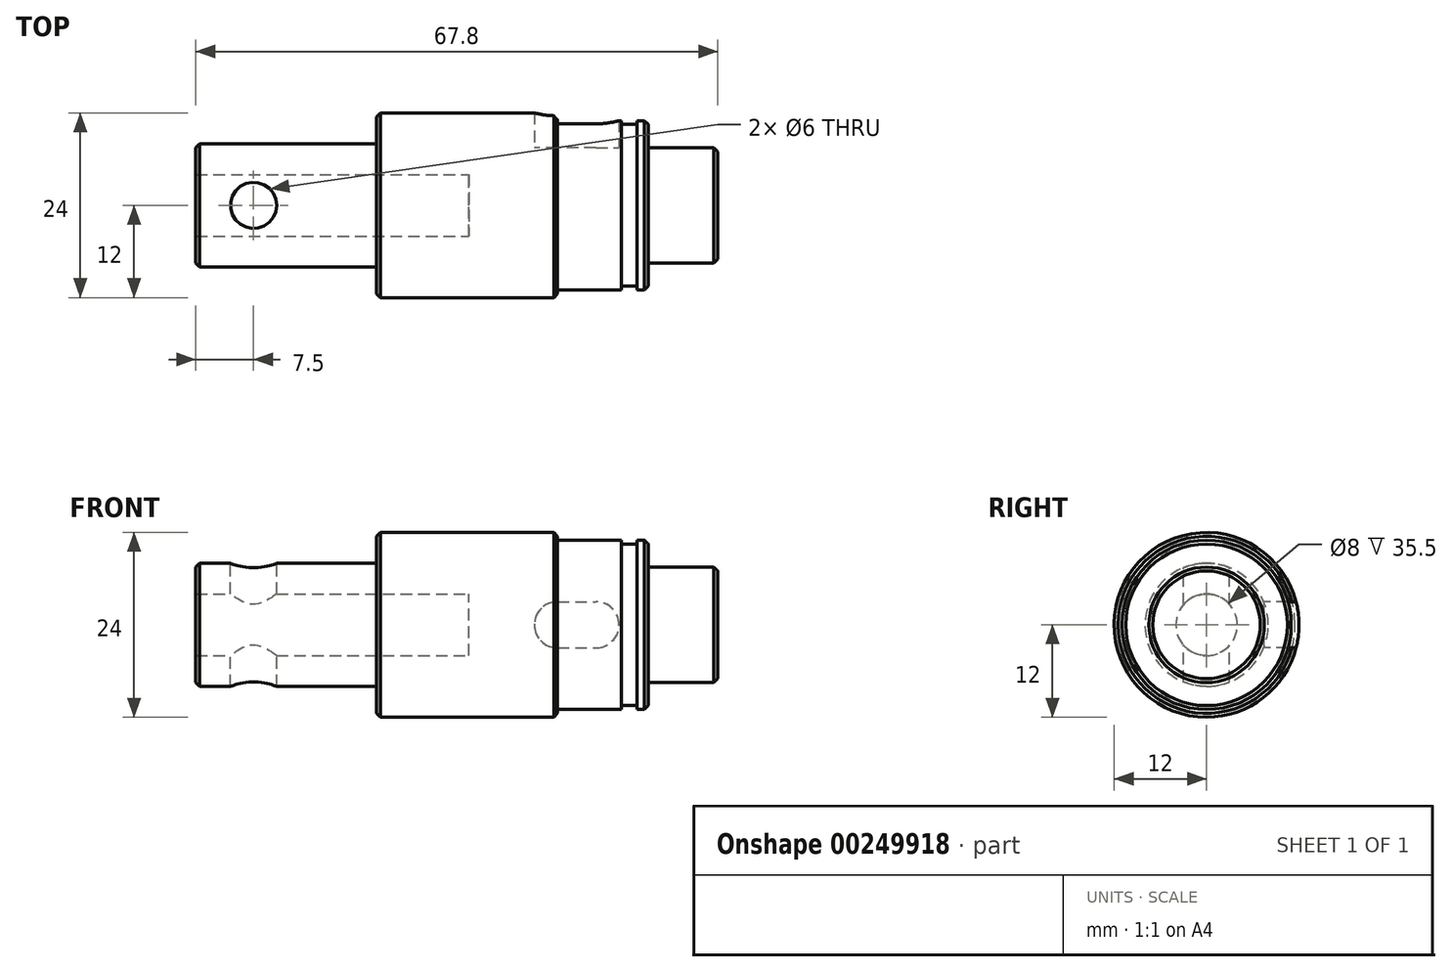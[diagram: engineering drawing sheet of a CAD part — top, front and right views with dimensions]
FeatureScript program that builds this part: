
annotation { "Feature Type Name" : "Feature", "Feature Type Description" : "" }
export const myFeature = defineFeature(function(context is Context, id is Id, definition is map)
    precondition{}
    {
        {
            var Q0;
            Q0=qCreatedBy(makeId("Front.planeOp"),FACE);
            var sketch = newSketch(context, id + "F0", { "sketchPlane" : qUnion([Q0])});
            skLineSegment(sketch, "E0", {"start": v(0, 0) * mm, "end": v(0, 4) * mm});
            skLineSegment(sketch, "E1", {"start": v(0, 4) * mm, "end": v(-35.5, 4) * mm});
            skLineSegment(sketch, "E2", {"start": v(-35.5, 4) * mm, "end": v(-35.5, 8) * mm});
            skLineSegment(sketch, "E3", {"start": v(-35.5, 8) * mm, "end": v(-12, 8) * mm});
            skLineSegment(sketch, "E4", {"start": v(-12, 8) * mm, "end": v(-12, 12) * mm});
            skLineSegment(sketch, "E5", {"start": v(-12, 12) * mm, "end": v(11.5, 12) * mm});
            skLineSegment(sketch, "E6", {"start": v(11.5, 12) * mm, "end": v(11.5, 10.5) * mm});
            skLineSegment(sketch, "E7", {"start": v(11.5, 10.5) * mm, "end": v(23.3, 10.5) * mm});
            skLineSegment(sketch, "E8", {"start": v(32.3, 7.5) * mm, "end": v(32.3, 0) * mm});
            skLineSegment(sketch, "E9", {"start": v(32.3, 0) * mm, "end": v(0, 0) * mm});
            skLineSegment(sketch, "E10", {"start": v(23.3, 10.5) * mm, "end": v(23.3, 7.5) * mm});
            skLineSegment(sketch, "E11", {"start": v(23.3, 7.5) * mm, "end": v(32.3, 7.5) * mm});
            skSolve(sketch);
        }
        {
            var Q0;
            Q0=makeQuery(id+"F0.imprint","IMPRINT",FACE,{"disambiguationData":[TD([[makeQuery(id+"F0.imprint","IMPRINT",EDGE,{"derivedFrom":sQuery(id+"F0.wireOp",EDGE,"E0")}),-1.0]])]});
            var Q1;
            Q1=sQuery(id+"F0.wireOp",EDGE,"E9");
            revolve(context, id + "F1", {"entities" : qUnion([Q0]), "axis" : qUnion([Q1]), "revolveType" : RevolveType.FULL});
        }
        {
            var Q0;
            Q0=makeQuery(id+"F1.opRevolve","SWEPT_EDGE",EDGE,{"disambiguationData":[OSD([sQuery(id+"F0.wireOp",EDGE,"E4"),sQuery(id+"F0.wireOp",EDGE,"E5")])]});
            chamfer(context, id + "F2", {"entities" : qUnion([Q0]), "width" : .5 * mm, "tangentPropagation" : true});
        }
        {
            var Q0;
            Q0=makeQuery(id+"F1.opRevolve","SWEPT_FACE",FACE,{"disambiguationData":[OSD([sQuery(id+"F0.wireOp",EDGE,"E10")])]});
            var sketch = newSketch(context, id + "F3", { "sketchPlane" : qUnion([Q0])});
            skCircle(sketch, "E12.0", {"center": v(0, 0) * mm, "radius": 10.5 * mm});
            skCircle(sketch, "E13", {"center": v(0, 0) * mm, "radius": 11 * mm});
            skSolve(sketch);
        }
        {
            var Q0;
            Q0 = qSketchRegion(id + "F3", true);
            extrude(context, id + "F4", {"entities" : qUnion([Q0]), "operationType" : NewBodyOperationType.ADD, "oppositeDirection" : true, "depth" : 1.5 * mm});
        }
        {
            var Q0;
            Q0=makeQuery(id+"F4.opExtrude","CAP_FACE",FACE,{"disambiguationData":[OSD([sQuery(id+"F3.wireOp",EDGE,"E12.0"),sQuery(id+"F3.wireOp",EDGE,"E13")])],"isStart":false});
            cPlane(context, id + "F5", {"entities" : qUnion([Q0]), "cplaneType" : CPlaneType.OFFSET, "offset" : 2 * mm, "width" : 150 * mm, "height" : 150 * mm});
        }
        {
            var Q0;
            Q0=qCreatedBy(id+"F5.planeOp",FACE);
            var sketch = newSketch(context, id + "F6", { "sketchPlane" : qUnion([Q0])});
            skCircle(sketch, "E14.0", {"center": v(0, 0) * mm, "radius": 11 * mm});
            skCircle(sketch, "E15.0", {"center": v(0, 0) * mm, "radius": 10.5 * mm});
            skSolve(sketch);
        }
        {
            var Q0;
            Q0 = qSketchRegion(id + "F6", true);
            var Q1;
            Q1=makeQuery(id+"F1.opRevolve","SWEPT_FACE",FACE,{"disambiguationData":[OSD([sQuery(id+"F0.wireOp",EDGE,"E6")])]});
            extrude(context, id + "F7", {"entities" : qUnion([Q0]), "operationType" : NewBodyOperationType.ADD, "endBound" : BoundingType.UP_TO_SURFACE, "endBoundEntityFace" : qUnion([Q1]), "depth" : 25 * mm});
        }
        {
            var Q0;
            Q0=makeQuery(id+"F1.opRevolve","SWEPT_EDGE",EDGE,{"disambiguationData":[OSD([sQuery(id+"F0.wireOp",EDGE,"E8"),sQuery(id+"F0.wireOp",EDGE,"E11")])]});
            var Q1;
            Q1=makeQuery(id+"F4.opExtrude","CAP_EDGE",EDGE,{"disambiguationData":[OSD([sQuery(id+"F3.wireOp",EDGE,"E13")])],"isStart":true});
            var Q2;
            Q2=makeQuery(id+"F1.opRevolve","SWEPT_EDGE",EDGE,{"disambiguationData":[OSD([sQuery(id+"F0.wireOp",EDGE,"E5"),sQuery(id+"F0.wireOp",EDGE,"E6")])]});
            var Q3;
            Q3=makeQuery(id+"F1.opRevolve","SWEPT_EDGE",EDGE,{"disambiguationData":[OSD([sQuery(id+"F0.wireOp",EDGE,"E2"),sQuery(id+"F0.wireOp",EDGE,"E3")])]});
            chamfer(context, id + "F8", {"entities" : qUnion([Q0, Q1, Q2, Q3]), "width" : .5 * mm, "tangentPropagation" : true});
        }
        {
            var Q0;
            Q0=qCreatedBy(makeId("Front.planeOp"),FACE);
            cPlane(context, id + "F9", {"entities" : qUnion([Q0]), "cplaneType" : CPlaneType.OFFSET, "offset" : 7.5 * mm, "oppositeDirection" : true, "width" : 150 * mm, "height" : 150 * mm});
        }
        {
            var Q0;
            Q0=qCreatedBy(id+"F9.planeOp",FACE);
            var sketch = newSketch(context, id + "F10", { "sketchPlane" : qUnion([Q0])});
            skArc(sketch, "E16", {"start": v(16.5, -3) * mm, "mid": v(19.5, 0) * mm, "end": v(16.5, 3) * mm});
            skArc(sketch, "E17", {"start": v(11.5, 3) * mm, "mid": v(8.5, 0) * mm, "end": v(11.5, -3) * mm});
            skPoint(sketch, "E18.orphan", {"position": v(11, 12) * mm});
            skPoint(sketch, "E19.0.start.orphan", {"position": v(11, -12) * mm});
            skLineSegment(sketch, "E20", {"start": v(16.5, 3) * mm, "end": v(11.5, 3) * mm});
            skLineSegment(sketch, "E21", {"start": v(16.5, -3) * mm, "end": v(11.5, -3) * mm});
            skSolve(sketch);
        }
        {
            var Q0;
            Q0 = qSketchRegion(id + "F10", true);
            extrude(context, id + "F11", {"entities" : qUnion([Q0]), "operationType" : NewBodyOperationType.REMOVE, "oppositeDirection" : true, "depth" : 25 * mm});
        }
        {
            var Q0;
            Q0=qCreatedBy(makeId("Top.planeOp"),FACE);
            var sketch = newSketch(context, id + "F12", { "sketchPlane" : qUnion([Q0])});
            skCircle(sketch, "E22", {"center": v(-28, 0) * mm, "radius": 3 * mm});
            skSolve(sketch);
        }
        {
            var Q0;
            Q0 = qSketchRegion(id + "F12", true);
            extrude(context, id + "F13", {"entities" : qUnion([Q0]), "operationType" : NewBodyOperationType.REMOVE, "endBound" : BoundingType.SYMMETRIC, "oppositeDirection" : true, "depth" : 25 * mm});
        }
    });
